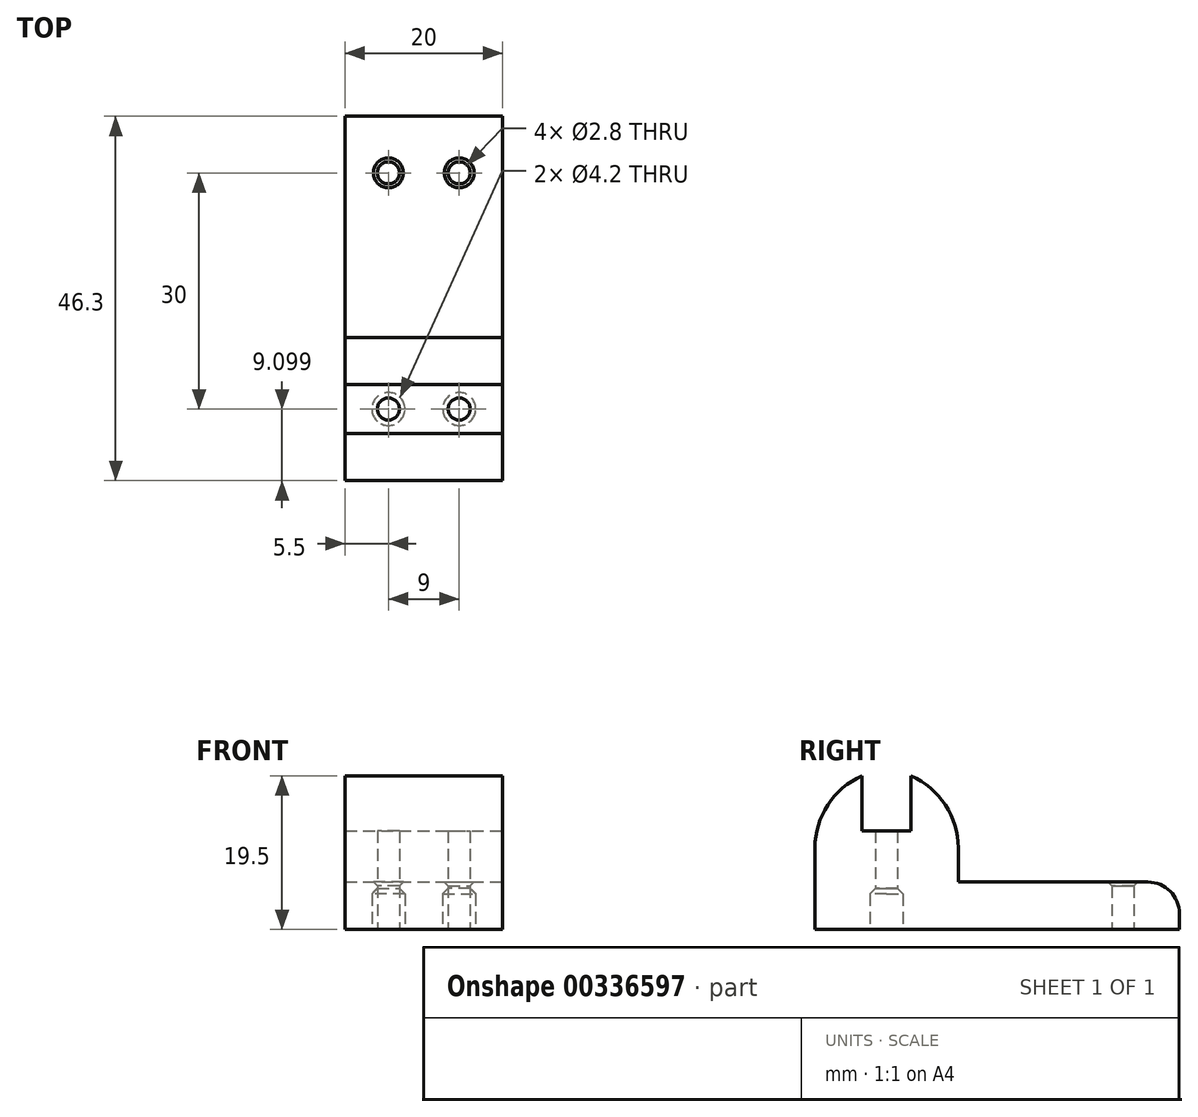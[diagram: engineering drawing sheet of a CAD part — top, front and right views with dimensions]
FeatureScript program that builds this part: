
annotation { "Feature Type Name" : "Feature", "Feature Type Description" : "" }
export const myFeature = defineFeature(function(context is Context, id is Id, definition is map)
    precondition{}
    {
        {
            var Q0;
            Q0=qCreatedBy(makeId("Top.planeOp"),FACE);
            var sketch = newSketch(context, id + "F0", { "sketchPlane" : qUnion([Q0])});
            skLineSegment(sketch, "E0.bottom", {"start": v(-10, 2.79) * mm, "end": v(0, 2.79) * mm});
            skLineSegment(sketch, "E0.top", {"start": v(-10, -43.51) * mm, "end": v(0, -43.51) * mm});
            skLineSegment(sketch, "E0.left", {"start": v(-10, 2.79) * mm, "end": v(-10, -43.51) * mm});
            skLineSegment(sketch, "E0.right", {"start": v(0, 2.79) * mm, "end": v(0, -43.51) * mm});
            skCircle(sketch, "E1", {"center": v(-4.5, -34.41) * mm, "radius": 1.4 * mm});
            skCircle(sketch, "E2", {"center": v(-4.5, -4.41) * mm, "radius": 1.4 * mm});
            skLineSegment(sketch, "E3", {"start": v(-10, -25.31) * mm, "end": v(0, -25.31) * mm});
            skLineSegment(sketch, "E4", {"start": v(-10, -31.31) * mm, "end": v(0, -31.31) * mm});
            skLineSegment(sketch, "E5", {"start": v(-10, -37.51) * mm, "end": v(0, -37.51) * mm});
            skCircle(sketch, "E6", {"center": v(-4.5, -34.41) * mm, "radius": 2.1 * mm});
            skSolve(sketch);
        }
        {
            var Q0;
            {var subQ0=sQuery(id+"F0.wireOp",EDGE,"E0.bottom");Q0=makeQuery(id+"F0.imprint","IMPRINT",FACE,{"disambiguationData":[TD([[makeQuery(id+"F0.imprint","IMPRINT",EDGE,{"derivedFrom":subQ0}),-1.0]])]});}
            extrude(context, id + "F1", {"entities" : qUnion([Q0]), "depth" : 6 * mm});
        }
        {
            var Q0;
            {var subQ0=sQuery(id+"F0.wireOp",EDGE,"E3");Q0=makeQuery(id+"F0.imprint","IMPRINT",FACE,{"disambiguationData":[TD([[makeQuery(id+"F0.imprint","IMPRINT",EDGE,{"derivedFrom":subQ0}),-1.0]])]});}
            extrude(context, id + "F2", {"entities" : qUnion([Q0]), "operationType" : NewBodyOperationType.ADD, "depth" : 19.5 * mm});
        }
        {
            var Q0;
            {var subQ0=sQuery(id+"F0.wireOp",EDGE,"E4");Q0=makeQuery(id+"F0.imprint","IMPRINT",FACE,{"disambiguationData":[TD([[makeQuery(id+"F0.imprint","IMPRINT",EDGE,{"derivedFrom":subQ0}),-1.0]])]});}
            extrude(context, id + "F3", {"entities" : qUnion([Q0]), "operationType" : NewBodyOperationType.ADD, "depth" : 12.5 * mm});
        }
        {
            var Q0;
            {var subQ0=sQuery(id+"F0.wireOp",EDGE,"E0.top");Q0=makeQuery(id+"F0.imprint","IMPRINT",FACE,{"disambiguationData":[TD([[makeQuery(id+"F0.imprint","IMPRINT",EDGE,{"derivedFrom":subQ0}),1.0]])]});}
            extrude(context, id + "F4", {"entities" : qUnion([Q0]), "operationType" : NewBodyOperationType.ADD, "depth" : 19.5 * mm});
        }
        {
            var Q0;
            Q0=makeQuery(id+"F0.imprint","IMPRINT",FACE,{"disambiguationData":[TD([[makeQuery(id+"F0.imprint","IMPRINT",EDGE,{"derivedFrom":sQuery(id+"F0.wireOp",EDGE,"E1")}),-1.0]])]});
            extrude(context, id + "F5", {"entities" : qUnion([Q0]), "operationType" : NewBodyOperationType.ADD, "depth" : 12.5 * mm});
        }
        {
            var Q0;
            Q0=makeQuery(id+"F0.imprint","IMPRINT",FACE,{"disambiguationData":[TD([[makeQuery(id+"F0.imprint","IMPRINT",EDGE,{"derivedFrom":sQuery(id+"F0.wireOp",EDGE,"E1")}),-1.0]])]});
            extrude(context, id + "F6", {"entities" : qUnion([Q0]), "operationType" : NewBodyOperationType.REMOVE, "depth" : 6.5 * mm});
        }
        {
            var Q0;
            Q0=makeQuery(id+"F2.opExtrude","CAP_EDGE",EDGE,{"disambiguationData":[OSD([sQuery(id+"F0.wireOp",EDGE,"E3")])],"isStart":false});
            var Q1;
            Q1=makeQuery(id+"F4.opExtrude","CAP_EDGE",EDGE,{"disambiguationData":[OSD([sQuery(id+"F0.wireOp",EDGE,"E0.top")])],"isStart":false});
            fillet(context, id + "F7", {"entities" : qUnion([Q0, Q1]), "radius" : 10 * mm, "tangentPropagation" : true, "allowEdgeOverflow" : false});
        }
        {
            var Q0;
            Q0=makeQuery(id+"F6.boolean.opBoolean","COPY",EDGE,{"derivedFrom":makeQuery(id+"F6.opExtrude","CAP_EDGE",EDGE,{"disambiguationData":[OSD([sQuery(id+"F0.wireOp",EDGE,"E6")])],"isStart":false})});
            chamfer(context, id + "F8", {"entities" : qUnion([Q0]), "width" : 2 * mm, "tangentPropagation" : true});
        }
        {
            var Q0;
            Q0=makeQuery(id+"F1.opExtrude","CAP_EDGE",EDGE,{"disambiguationData":[OSD([sQuery(id+"F0.wireOp",EDGE,"E0.bottom")])],"isStart":false});
            fillet(context, id + "F9", {"entities" : qUnion([Q0]), "radius" : 4 * mm, "tangentPropagation" : true, "allowEdgeOverflow" : false});
        }
        {
            var Q0;
            Q0=makeQuery(id+"F1.opExtrude","CAP_EDGE",EDGE,{"disambiguationData":[OSD([sQuery(id+"F0.wireOp",EDGE,"E2")])],"isStart":false});
            chamfer(context, id + "F10", {"entities" : qUnion([Q0]), "width" : .5 * mm, "tangentPropagation" : true});
        }
        {
            var Q0;
            Q0=makeQuery(id+"F1.opExtrude","SWEPT_BODY",BODY,{"disambiguationData":[OSD([sQuery(id+"F0.wireOp",EDGE,"E0.bottom"),sQuery(id+"F0.wireOp",EDGE,"E0.left"),sQuery(id+"F0.wireOp",EDGE,"E0.right"),sQuery(id+"F0.wireOp",EDGE,"E2"),sQuery(id+"F0.wireOp",EDGE,"E3")])]});
            var Q1;
            Q1=qCreatedBy(makeId("Right.planeOp"),FACE);
            mirror(context, id + "F11", {"operationType" : NewBodyOperationType.ADD, "entities" : qUnion([Q0]), "mirrorPlane" : qUnion([Q1])});
        }
    });
